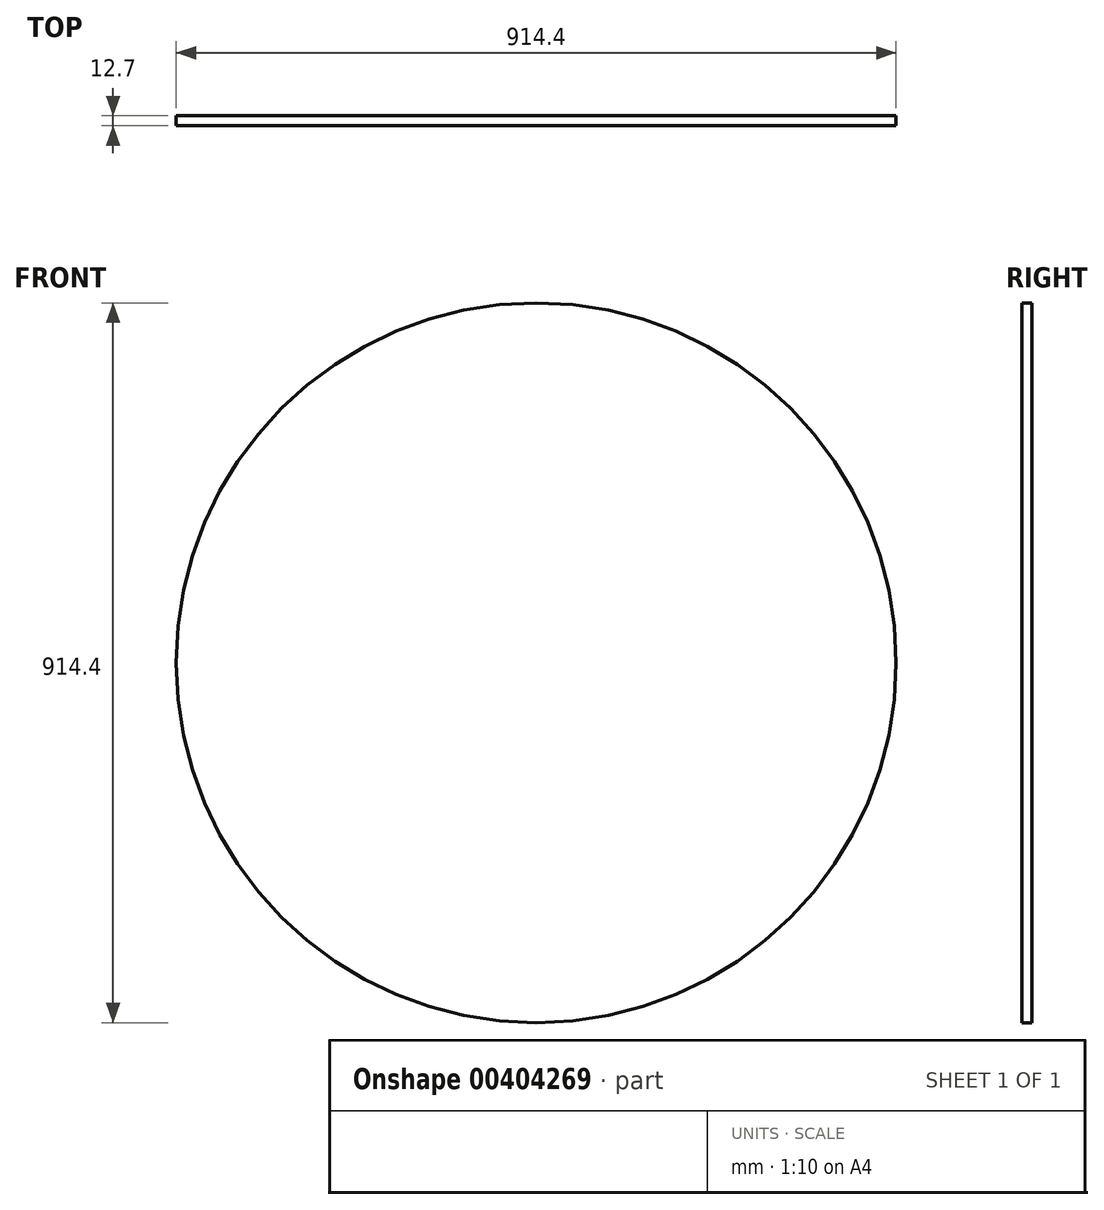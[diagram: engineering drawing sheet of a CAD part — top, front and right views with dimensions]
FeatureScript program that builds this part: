
annotation { "Feature Type Name" : "Feature", "Feature Type Description" : "" }
export const myFeature = defineFeature(function(context is Context, id is Id, definition is map)
    precondition{}
    {
        {
            var Q0;
            Q0=qCreatedBy(makeId("Front.planeOp"),FACE);
            var sketch = newSketch(context, id + "F0", { "sketchPlane" : qUnion([Q0])});
            skCircle(sketch, "E0", {"center": v(0, 0) * mm, "radius": 457.2 * mm});
            skSolve(sketch);
        }
        {
            var Q0;
            Q0 = qSketchRegion(id + "F0", true);
            extrude(context, id + "F1", {"entities" : qUnion([Q0]), "depth" : 25.4 * mm});
        }
        {
            var Q0;
            Q0=makeQuery(id+"F1.opExtrude","CAP_FACE",FACE,{"disambiguationData":[OSD([sQuery(id+"F0.wireOp",EDGE,"E0")])],"isStart":false});
            extrude(context, id + "F2", {"entities" : qUnion([Q0]), "operationType" : NewBodyOperationType.REMOVE, "oppositeDirection" : true, "depth" : 12.7 * mm});
        }
    });
